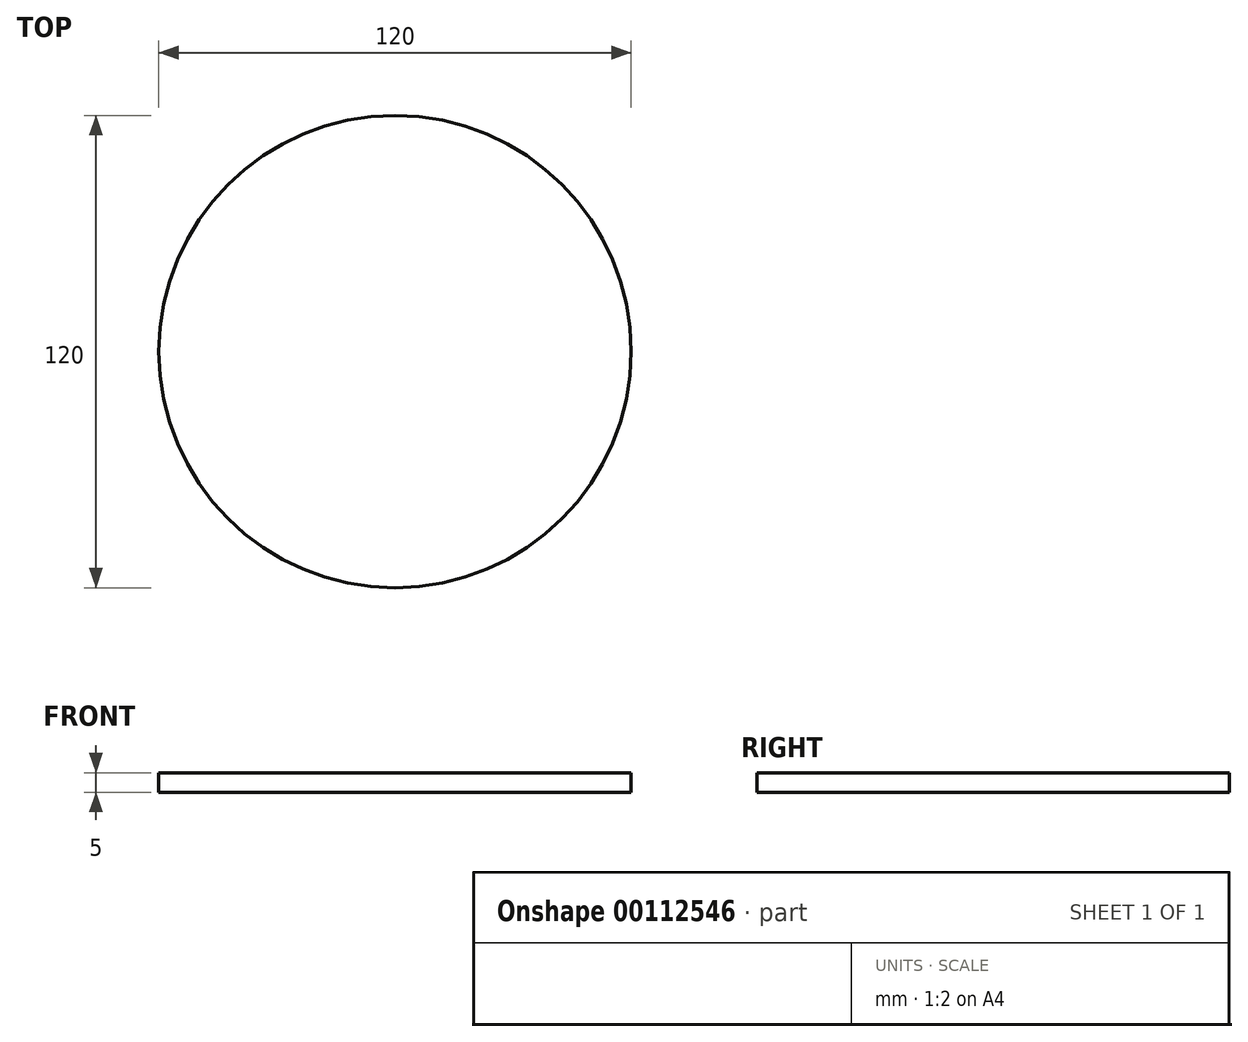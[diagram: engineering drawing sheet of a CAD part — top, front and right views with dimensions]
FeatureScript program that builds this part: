
annotation { "Feature Type Name" : "Feature", "Feature Type Description" : "" }
export const myFeature = defineFeature(function(context is Context, id is Id, definition is map)
    precondition{}
    {
        {
            var Q0;
            Q0=qCreatedBy(makeId("Top.planeOp"),FACE);
            var sketch = newSketch(context, id + "F0", { "sketchPlane" : qUnion([Q0])});
            skCircle(sketch, "E0", {"center": v(0, 0) * mm, "radius": 20 * mm});
            skCircle(sketch, "E1", {"center": v(0, 0) * mm, "radius": 60 * mm});
            skSolve(sketch);
        }
        {
            var Q0;
            Q0=makeQuery(id+"F0.imprint","IMPRINT",FACE,{"disambiguationData":[TD([[makeQuery(id+"F0.imprint","IMPRINT",EDGE,{"derivedFrom":sQuery(id+"F0.wireOp",EDGE,"E0")}),1.0]])]});
            var Q1;
            Q1=makeQuery(id+"F0.imprint","IMPRINT",FACE,{"disambiguationData":[TD([[makeQuery(id+"F0.imprint","IMPRINT",EDGE,{"derivedFrom":sQuery(id+"F0.wireOp",EDGE,"E0")}),-1.0]])]});
            extrude(context, id + "F1", {"entities" : qUnion([Q0, Q1]), "depth" : 5 * mm});
        }
    });
